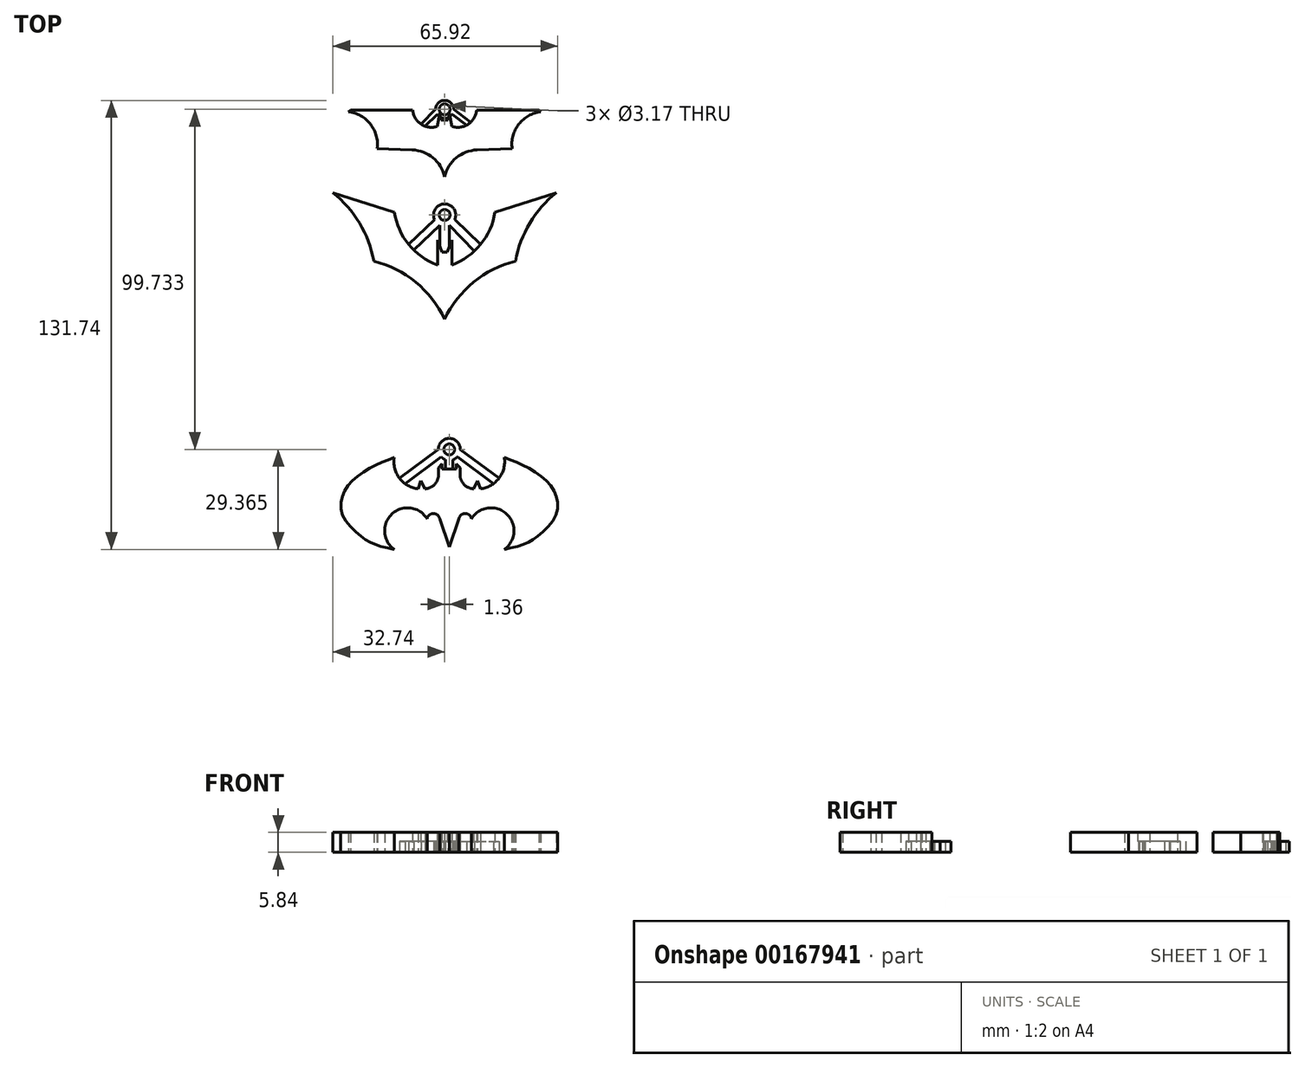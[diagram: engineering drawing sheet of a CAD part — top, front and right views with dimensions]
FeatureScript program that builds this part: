
annotation { "Feature Type Name" : "Feature", "Feature Type Description" : "" }
export const myFeature = defineFeature(function(context is Context, id is Id, definition is map)
    precondition{}
    {
        {
            var Q0;
            Q0=qCreatedBy(makeId("Top.planeOp"),FACE);
            var sketch = newSketch(context, id + "F0", { "sketchPlane" : qUnion([Q0])});
            skLineSegment(sketch, "E0", {"start": v(-61.27, 59.07) * mm, "end": v(-43, 59.07) * mm});
            skLineSegment(sketch, "E1", {"start": v(-61.27, 59.07) * mm, "end": v(-61.85, 58.53) * mm});
            skArc(sketch, "E2", {"start": v(-43, 59.07) * mm, "mid": v(-40.56, 54.9) * mm, "end": v(-35.78, 54.25) * mm});
            skArc(sketch, "E3", {"start": v(-53.42, 47.7) * mm, "mid": v(-55.35, 54.9) * mm, "end": v(-61.85, 58.53) * mm});
            skLineSegment(sketch, "E4", {"start": v(-53.42, 47.7) * mm, "end": v(-43.13, 47.35) * mm});
            skLineSegment(sketch, "E5", {"start": v(-35.04, 58.07) * mm, "end": v(-35.78, 54.25) * mm});
            skLineSegment(sketch, "E6", {"start": v(-35.04, 58.07) * mm, "end": v(-34.61, 56.16) * mm});
            skArc(sketch, "E7.MirrorCS", {"start": v(-13.84, 47.7) * mm, "mid": v(-11.9, 54.9) * mm, "end": v(-5.4, 58.53) * mm});
            skLineSegment(sketch, "E8.MirrorCS", {"start": v(-6, 59.07) * mm, "end": v(-5.4, 58.53) * mm});
            skArc(sketch, "E9.MirrorCS", {"start": v(-24.26, 59.07) * mm, "mid": v(-26.7, 54.9) * mm, "end": v(-31.47, 54.25) * mm});
            skLineSegment(sketch, "E10.MirrorCS", {"start": v(-32.21, 58.07) * mm, "end": v(-31.47, 54.25) * mm});
            skLineSegment(sketch, "E11.MirrorCS", {"start": v(-32.21, 58.07) * mm, "end": v(-32.64, 56.16) * mm});
            skLineSegment(sketch, "E12.MirrorCS", {"start": v(-13.84, 47.7) * mm, "end": v(-24.12, 47.35) * mm});
            skLineSegment(sketch, "E13", {"start": v(-48.38, 29.1) * mm, "end": v(-66.37, 34.83) * mm});
            skArc(sketch, "E14", {"start": v(-48.38, 29.1) * mm, "mid": v(-44.18, 19.62) * mm, "end": v(-35.72, 13.62) * mm});
            skArc(sketch, "E15", {"start": v(-54.4, 14.73) * mm, "mid": v(-58.58, 25.86) * mm, "end": v(-66.37, 34.83) * mm});
            skArc(sketch, "E16", {"start": v(-33.63, -2.3) * mm, "mid": v(-42.11, 8.54) * mm, "end": v(-54.4, 14.73) * mm});
            skLineSegment(sketch, "E17", {"start": v(-35.72, 13.62) * mm, "end": v(-35.72, 20.96) * mm});
            skLineSegment(sketch, "E18", {"start": v(-35.72, 20.96) * mm, "end": v(-34.4, 17.36) * mm});
            skLineSegment(sketch, "E19", {"start": v(-34.4, 17.36) * mm, "end": v(-33.63, 17.36) * mm});
            skLineSegment(sketch, "E20.MirrorCS", {"start": v(-31.54, 20.96) * mm, "end": v(-32.85, 17.36) * mm});
            skLineSegment(sketch, "E21.MirrorCS", {"start": v(-32.85, 17.36) * mm, "end": v(-33.63, 17.36) * mm});
            skLineSegment(sketch, "E22.MirrorCS", {"start": v(-31.54, 13.62) * mm, "end": v(-31.54, 20.96) * mm});
            skArc(sketch, "E23.MirrorCS", {"start": v(-18.88, 29.1) * mm, "mid": v(-23.08, 19.62) * mm, "end": v(-31.54, 13.62) * mm});
            skLineSegment(sketch, "E24.MirrorCS", {"start": v(-18.88, 29.1) * mm, "end": v(-0.89, 34.83) * mm});
            skArc(sketch, "E25.MirrorCS", {"start": v(-12.86, 14.73) * mm, "mid": v(-8.68, 25.86) * mm, "end": v(-0.89, 34.83) * mm});
            skArc(sketch, "E26.MirrorCS", {"start": v(-33.63, -2.3) * mm, "mid": v(-25.15, 8.54) * mm, "end": v(-12.86, 14.73) * mm});
            skFitSpline(sketch, "E27", {"points": [v(-48.41, -42.87) * mm, v(-54.5, -45.44) * mm, v(-60.68, -49.68) * mm, v(-63.75, -54.6) * mm, v(-63.34, -60.23) * mm, v(-58.34, -65.83) * mm, v(-54.55, -68.22) * mm, v(-48.37, -69.86) * mm], "startDerivative": vector(-40.98, -15.49) * mm, "endDerivative": vector(46.5, -9.89) * mm});
            skArc(sketch, "E28", {"start": v(-38.76, -60.87) * mm, "mid": v(-49.1, -59.45) * mm, "end": v(-48.37, -69.86) * mm});
            skLineSegment(sketch, "E29", {"start": v(-41.38, -52.07) * mm, "end": v(-40.57, -49.73) * mm});
            skLineSegment(sketch, "E30", {"start": v(-40.57, -49.73) * mm, "end": v(-39.4, -52.07) * mm});
            skArc(sketch, "E31", {"start": v(-35.1, -60.87) * mm, "mid": v(-36.94, -59.3) * mm, "end": v(-38.76, -60.87) * mm});
            skLineSegment(sketch, "E32", {"start": v(-35.1, -60.87) * mm, "end": v(-32.27, -69.07) * mm});
            skArc(sketch, "E33", {"start": v(-39.4, -52.07) * mm, "mid": v(-36.43, -50.62) * mm, "end": v(-35.47, -47.47) * mm});
            skLineSegment(sketch, "E34", {"start": v(-35.47, -47.47) * mm, "end": v(-35.47, -45.85) * mm});
            skLineSegment(sketch, "E35", {"start": v(-35.47, -45.85) * mm, "end": v(-34.39, -44.67) * mm});
            skLineSegment(sketch, "E36", {"start": v(-34.39, -44.67) * mm, "end": v(-34.39, -46.25) * mm});
            skCircle(sketch, "E37", {"center": v(-33.63, 28.27) * mm, "radius": 1.59 * mm});
            skCircle(sketch, "E38", {"center": v(-32.27, -40.5) * mm, "radius": 1.59 * mm});
            skLineSegment(sketch, "E39", {"start": v(-36.6, 26.94) * mm, "end": v(-44.18, 19.62) * mm});
            skLineSegment(sketch, "E40", {"start": v(-30.66, 26.94) * mm, "end": v(-23.08, 19.62) * mm});
            skLineSegment(sketch, "E41", {"start": v(-35.06, 25.3) * mm, "end": v(-42.66, 17.97) * mm});
            skLineSegment(sketch, "E42", {"start": v(-32.3, 25.3) * mm, "end": v(-24.93, 17.66) * mm});
            skLineSegment(sketch, "E43", {"start": v(-35.06, 25.3) * mm, "end": v(-35.06, 19.15) * mm});
            skLineSegment(sketch, "E44", {"start": v(-32.3, 25.3) * mm, "end": v(-32.3, 18.87) * mm});
            skPoint(sketch, "E45.orphan", {"position": v(-33.63, 26.68) * mm});
            skPoint(sketch, "E46.orphan", {"position": v(-32.04, 28.27) * mm});
            skPoint(sketch, "E47.orphan", {"position": v(-35.22, 28.27) * mm});
            skArc(sketch, "E48", {"start": v(-30.66, 26.94) * mm, "mid": v(-33.63, 31.52) * mm, "end": v(-36.6, 26.94) * mm});
            skCircle(sketch, "E49", {"center": v(-33.63, 59.24) * mm, "radius": 1.59 * mm});
            skArc(sketch, "E50", {"start": v(-34.77, 56.86) * mm, "mid": v(-33.63, 56.6) * mm, "end": v(-32.49, 56.86) * mm});
            skLineSegment(sketch, "E51", {"start": v(-36.27, 59.24) * mm, "end": v(-40.56, 54.9) * mm});
            skLineSegment(sketch, "E52", {"start": v(-30.99, 59.24) * mm, "end": v(-25.98, 55.47) * mm});
            skLineSegment(sketch, "E53", {"start": v(-35.85, 57.8) * mm, "end": v(-39.33, 54.29) * mm});
            skLineSegment(sketch, "E54", {"start": v(-31.4, 57.8) * mm, "end": v(-27.17, 54.62) * mm});
            skArc(sketch, "E55.trimOffspring", {"start": v(-32.03, 57.13) * mm, "mid": v(-33.63, 61.88) * mm, "end": v(-35.23, 57.13) * mm});
            skPoint(sketch, "E56.start.orphan", {"position": v(-32.27, -43.72) * mm});
            skLineSegment(sketch, "E57", {"start": v(-24.26, 59.07) * mm, "end": v(-6, 59.07) * mm});
            skLineSegment(sketch, "E58", {"start": v(-34.61, 56.16) * mm, "end": v(-32.64, 56.16) * mm});
            skPoint(sketch, "E59.endSnap0", {"position": v(-33.63, 56.16) * mm});
            skArc(sketch, "E60", {"start": v(-24.12, 47.35) * mm, "mid": v(-30.21, 45.03) * mm, "end": v(-33.63, 39.48) * mm});
            skArc(sketch, "E61", {"start": v(-33.63, 39.48) * mm, "mid": v(-37.04, 45.03) * mm, "end": v(-43.13, 47.35) * mm});
            skArc(sketch, "E62", {"start": v(-48.41, -42.87) * mm, "mid": v(-46.85, -48.96) * mm, "end": v(-41.38, -52.07) * mm});
            skCircle(sketch, "E63", {"center": v(-32.27, -40.5) * mm, "radius": 3.23 * mm});
            skLineSegment(sketch, "E64.MirrorCS", {"start": v(-30.15, -44.67) * mm, "end": v(-30.15, -46.25) * mm});
            skLineSegment(sketch, "E65.MirrorCS", {"start": v(-29.07, -45.85) * mm, "end": v(-30.15, -44.67) * mm});
            skLineSegment(sketch, "E66.MirrorCS", {"start": v(-29.07, -47.47) * mm, "end": v(-29.07, -45.85) * mm});
            skArc(sketch, "E67.MirrorCS", {"start": v(-25.15, -52.07) * mm, "mid": v(-28.1, -50.62) * mm, "end": v(-29.07, -47.47) * mm});
            skLineSegment(sketch, "E68.MirrorCS", {"start": v(-29.43, -60.87) * mm, "end": v(-32.27, -69.07) * mm});
            skArc(sketch, "E69.MirrorCS", {"start": v(-29.43, -60.87) * mm, "mid": v(-27.6, -59.3) * mm, "end": v(-25.78, -60.87) * mm});
            skArc(sketch, "E70.MirrorCS", {"start": v(-25.78, -60.87) * mm, "mid": v(-15.44, -59.45) * mm, "end": v(-16.17, -69.86) * mm});
            skArc(sketch, "E71.MirrorCS", {"start": v(-16.13, -42.87) * mm, "mid": v(-17.7, -48.96) * mm, "end": v(-23.16, -52.07) * mm});
            skLineSegment(sketch, "E72.MirrorCS", {"start": v(-23.16, -52.07) * mm, "end": v(-23.97, -49.73) * mm});
            skLineSegment(sketch, "E73.MirrorCS", {"start": v(-23.97, -49.73) * mm, "end": v(-25.15, -52.07) * mm});
            skFitSpline(sketch, "E74.MirrorCS", {"points": [v(-16.13, -42.87) * mm, v(-10.04, -45.44) * mm, v(-3.86, -49.68) * mm, v(-0.8, -54.6) * mm, v(-1.2, -60.23) * mm, v(-6.2, -65.83) * mm, v(-10, -68.22) * mm, v(-16.17, -69.86) * mm], "startDerivative": vector(40.98, -15.49) * mm, "endDerivative": vector(-46.5, -9.89) * mm});
            skLineSegment(sketch, "E75", {"start": v(-35.5, -40.5) * mm, "end": v(-46.85, -48.96) * mm});
            skLineSegment(sketch, "E76", {"start": v(-34.67, -42.65) * mm, "end": v(-45.25, -50.54) * mm});
            skLineSegment(sketch, "E77", {"start": v(-29.04, -40.5) * mm, "end": v(-17.7, -48.96) * mm});
            skLineSegment(sketch, "E78", {"start": v(-29.87, -42.65) * mm, "end": v(-19.3, -50.54) * mm});
            skLineSegment(sketch, "E79", {"start": v(-33.36, -43.53) * mm, "end": v(-33.36, -46.25) * mm});
            skLineSegment(sketch, "E80", {"start": v(-34.39, -46.25) * mm, "end": v(-30.15, -46.25) * mm});
            skLineSegment(sketch, "E81", {"start": v(-31.18, -43.53) * mm, "end": v(-31.18, -46.25) * mm});
            skSolve(sketch);
        }
        {
            var Q0;
            {var subQ20=sQuery(id+"F0.wireOp",EDGE,"E0");Q0=makeQuery(id+"F0.imprint","IMPRINT",FACE,{"disambiguationData":[TD([[makeQuery(id+"F0.imprint","IMPRINT",EDGE,{"derivedFrom":subQ20}),-1.0]])]});}
            var Q1;
            {var subQ15=sQuery(id+"F0.wireOp",EDGE,"E13");Q1=makeQuery(id+"F0.imprint","IMPRINT",FACE,{"disambiguationData":[TD([[makeQuery(id+"F0.imprint","IMPRINT",EDGE,{"derivedFrom":subQ15}),1.0]])]});}
            var Q2;
            {var subQ5=sQuery(id+"F0.wireOp",EDGE,"E27");Q2=makeQuery(id+"F0.imprint","IMPRINT",FACE,{"disambiguationData":[TD([[makeQuery(id+"F0.imprint","IMPRINT",EDGE,{"derivedFrom":subQ5}),1.0]])]});}
            extrude(context, id + "F1", {"entities" : qUnion([Q0, Q1, Q2]), "depth" : 5.84 * mm});
        }
        {
            var Q0;
            {var subQ0=sQuery(id+"F0.wireOp",EDGE,"E51");Q0=makeQuery(id+"F0.imprint","IMPRINT",FACE,{"disambiguationData":[TD([[makeQuery(id+"F0.imprint","IMPRINT",EDGE,{"derivedFrom":subQ0}),1.0]])]});}
            var Q1;
            {var subQ0=sQuery(id+"F0.wireOp",EDGE,"E52");Q1=makeQuery(id+"F0.imprint","IMPRINT",FACE,{"disambiguationData":[TD([[makeQuery(id+"F0.imprint","IMPRINT",EDGE,{"derivedFrom":subQ0}),-1.0]])]});}
            var Q2;
            Q2=makeQuery(id+"F0.imprint","IMPRINT",FACE,{"disambiguationData":[TD([[makeQuery(id+"F0.imprint","IMPRINT",EDGE,{"derivedFrom":sQuery(id+"F0.wireOp",EDGE,"E49")}),-1.0]])]});
            extrude(context, id + "F2", {"entities" : qUnion([Q0, Q1, Q2]), "operationType" : NewBodyOperationType.ADD, "depth" : 3.17 * mm});
        }
        {
            var Q0;
            {var subQ3=sQuery(id+"F0.wireOp",EDGE,"E19");Q0=makeQuery(id+"F0.imprint","IMPRINT",FACE,{"disambiguationData":[TD([[makeQuery(id+"F0.imprint","IMPRINT",EDGE,{"derivedFrom":subQ3}),1.0]])]});}
            extrude(context, id + "F3", {"entities" : qUnion([Q0]), "operationType" : NewBodyOperationType.ADD, "depth" : 3.17 * mm});
        }
        {
            var Q0;
            {var subQ0=sQuery(id+"F0.wireOp",EDGE,"E77");Q0=makeQuery(id+"F0.imprint","IMPRINT",FACE,{"disambiguationData":[TD([[makeQuery(id+"F0.imprint","IMPRINT",EDGE,{"derivedFrom":subQ0}),-1.0]])]});}
            var Q1;
            {var subQ0=sQuery(id+"F0.wireOp",EDGE,"E75");Q1=makeQuery(id+"F0.imprint","IMPRINT",FACE,{"disambiguationData":[TD([[makeQuery(id+"F0.imprint","IMPRINT",EDGE,{"derivedFrom":subQ0}),1.0]])]});}
            var Q2;
            Q2=makeQuery(id+"F0.imprint","IMPRINT",FACE,{"disambiguationData":[TD([[makeQuery(id+"F0.imprint","IMPRINT",EDGE,{"derivedFrom":sQuery(id+"F0.wireOp",EDGE,"E38")}),-1.0]])]});
            var Q3;
            {var subQ0=sQuery(id+"F0.wireOp",EDGE,"E79");Q3=makeQuery(id+"F0.imprint","IMPRINT",FACE,{"disambiguationData":[TD([[makeQuery(id+"F0.imprint","IMPRINT",EDGE,{"derivedFrom":subQ0}),1.0]])]});}
            extrude(context, id + "F4", {"entities" : qUnion([Q0, Q1, Q2, Q3]), "operationType" : NewBodyOperationType.ADD, "depth" : 3.17 * mm});
        }
    });
